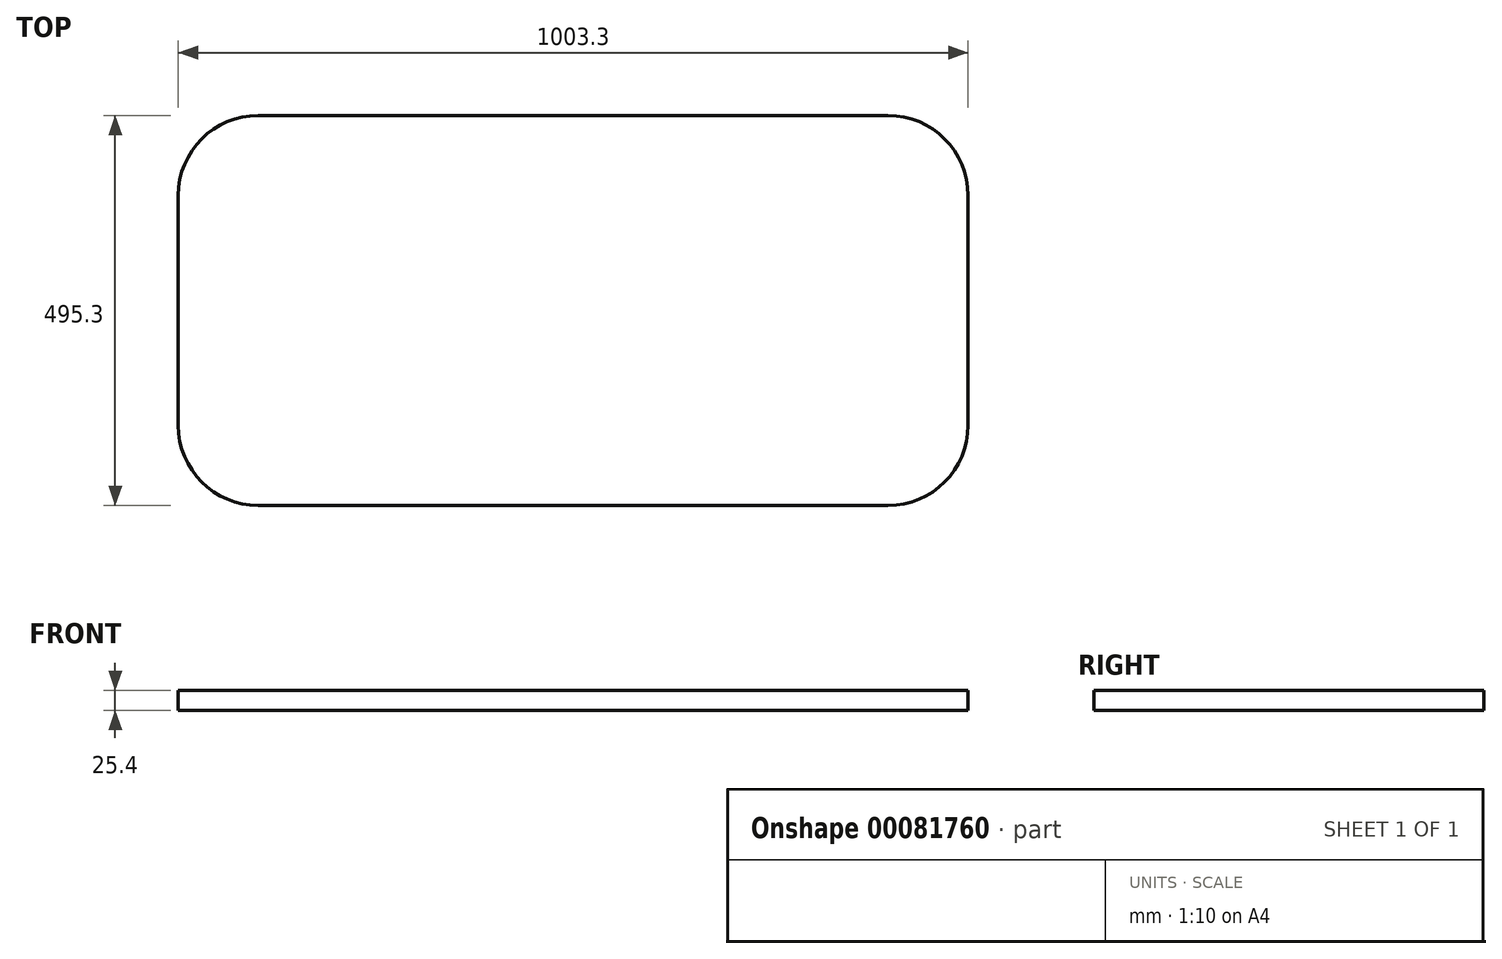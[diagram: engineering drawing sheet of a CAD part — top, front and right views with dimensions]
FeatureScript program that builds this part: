
annotation { "Feature Type Name" : "Feature", "Feature Type Description" : "" }
export const myFeature = defineFeature(function(context is Context, id is Id, definition is map)
    precondition{}
    {
        {
            var Q0;
            Q0=qCreatedBy(makeId("Top.planeOp"),FACE);
            var sketch = newSketch(context, id + "F0", { "sketchPlane" : qUnion([Q0])});
            skLineSegment(sketch, "E0.bottom", {"start": v(521.71, -247.65) * mm, "end": v(-481.59, -247.65) * mm});
            skLineSegment(sketch, "E0.top", {"start": v(521.71, 247.65) * mm, "end": v(-481.59, 247.65) * mm});
            skLineSegment(sketch, "E0.left", {"start": v(521.71, -247.65) * mm, "end": v(521.71, 247.65) * mm});
            skLineSegment(sketch, "E0.right", {"start": v(-481.59, -247.65) * mm, "end": v(-481.59, 247.65) * mm});
            skPoint(sketch, "E0.middle", {"position": v(20.06, 0) * mm});
            skSolve(sketch);
        }
        {
            var Q0;
            Q0 = qSketchRegion(id + "F0", true);
            extrude(context, id + "F1", {"entities" : qUnion([Q0]), "depth" : 25.4 * mm});
        }
        {
            var Q0;
            Q0=makeQuery(id+"F1.opExtrude","SWEPT_EDGE",EDGE,{"disambiguationData":[OSD([sQuery(id+"F0.wireOp",EDGE,"E0.bottom"),sQuery(id+"F0.wireOp",EDGE,"E0.right")])]});
            var Q1;
            Q1=makeQuery(id+"F1.opExtrude","SWEPT_EDGE",EDGE,{"disambiguationData":[OSD([sQuery(id+"F0.wireOp",EDGE,"E0.bottom"),sQuery(id+"F0.wireOp",EDGE,"E0.left")])]});
            var Q2;
            Q2=makeQuery(id+"F1.opExtrude","SWEPT_EDGE",EDGE,{"disambiguationData":[OSD([sQuery(id+"F0.wireOp",EDGE,"E0.top"),sQuery(id+"F0.wireOp",EDGE,"E0.left")])]});
            var Q3;
            Q3=makeQuery(id+"F1.opExtrude","SWEPT_EDGE",EDGE,{"disambiguationData":[OSD([sQuery(id+"F0.wireOp",EDGE,"E0.top"),sQuery(id+"F0.wireOp",EDGE,"E0.right")])]});
            fillet(context, id + "F2", {"entities" : qUnion([Q0, Q1, Q2, Q3]), "radius" : 101.6 * mm, "tangentPropagation" : true, "allowEdgeOverflow" : false});
        }
    });
